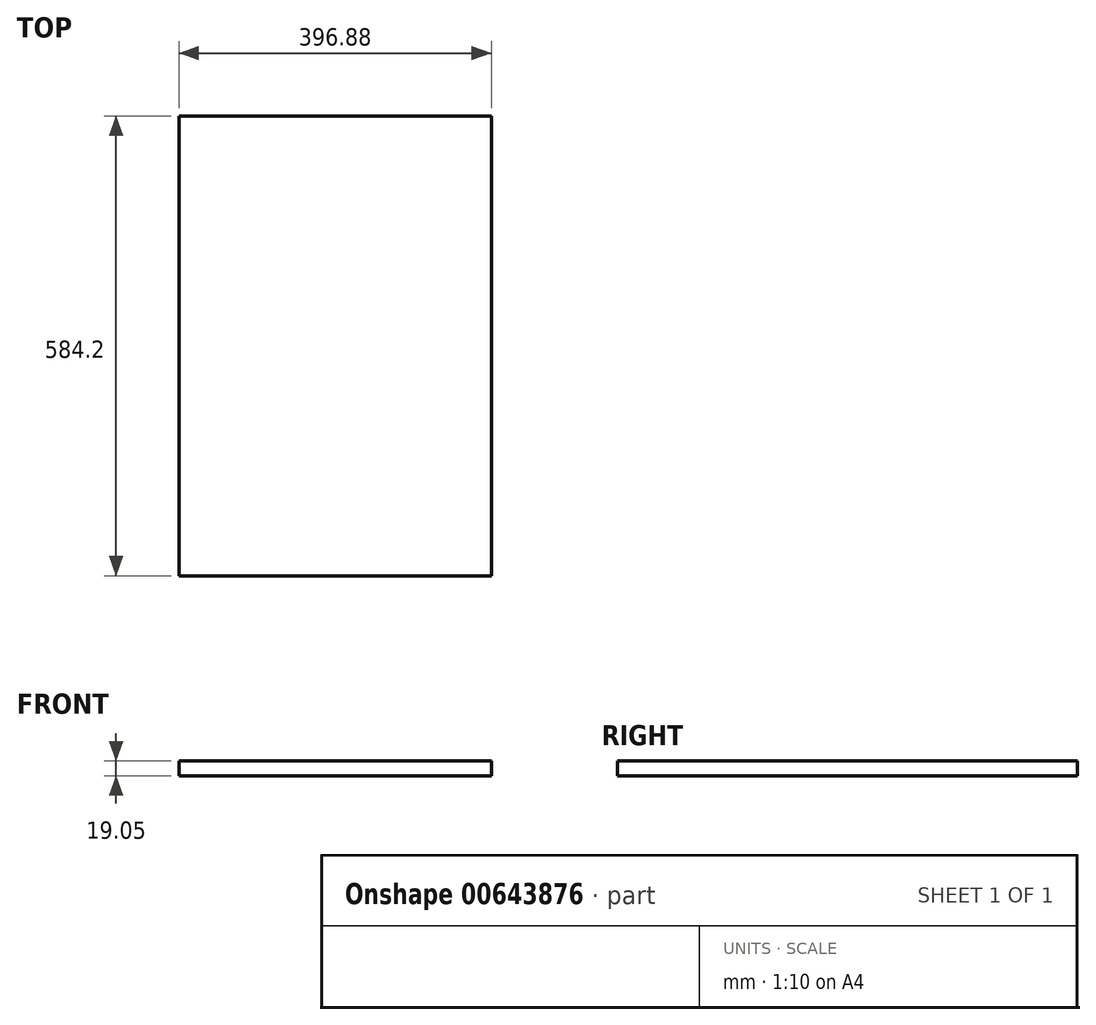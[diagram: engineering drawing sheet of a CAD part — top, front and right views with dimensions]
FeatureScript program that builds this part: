
annotation { "Feature Type Name" : "Feature", "Feature Type Description" : "" }
export const myFeature = defineFeature(function(context is Context, id is Id, definition is map)
    precondition{}
    {
        {
            var Q0;
            Q0=qCreatedBy(makeId("Top.planeOp"),FACE);
            var sketch = newSketch(context, id + "F0", { "sketchPlane" : qUnion([Q0])});
            skLineSegment(sketch, "E0.bottom", {"start": v(198.44, 292.1) * mm, "end": v(-198.44, 292.1) * mm});
            skLineSegment(sketch, "E0.top", {"start": v(198.44, -292.1) * mm, "end": v(-198.44, -292.1) * mm});
            skLineSegment(sketch, "E0.left", {"start": v(198.44, 292.1) * mm, "end": v(198.44, -292.1) * mm});
            skLineSegment(sketch, "E0.right", {"start": v(-198.44, 292.1) * mm, "end": v(-198.44, -292.1) * mm});
            skPoint(sketch, "E0.middle", {"position": v(0, 0) * mm});
            skSolve(sketch);
        }
        {
            var Q0;
            Q0=makeQuery(id+"F0.imprint","IMPRINT",FACE,{"disambiguationData":[TD([[makeQuery(id+"F0.imprint","IMPRINT",EDGE,{"derivedFrom":sQuery(id+"F0.wireOp",EDGE,"E0.bottom")}),1.0]])]});
            extrude(context, id + "F1", {"entities" : qUnion([Q0]), "depth" : 19.05 * mm, "offsetDistance" : 25.4 * mm});
        }
    });
